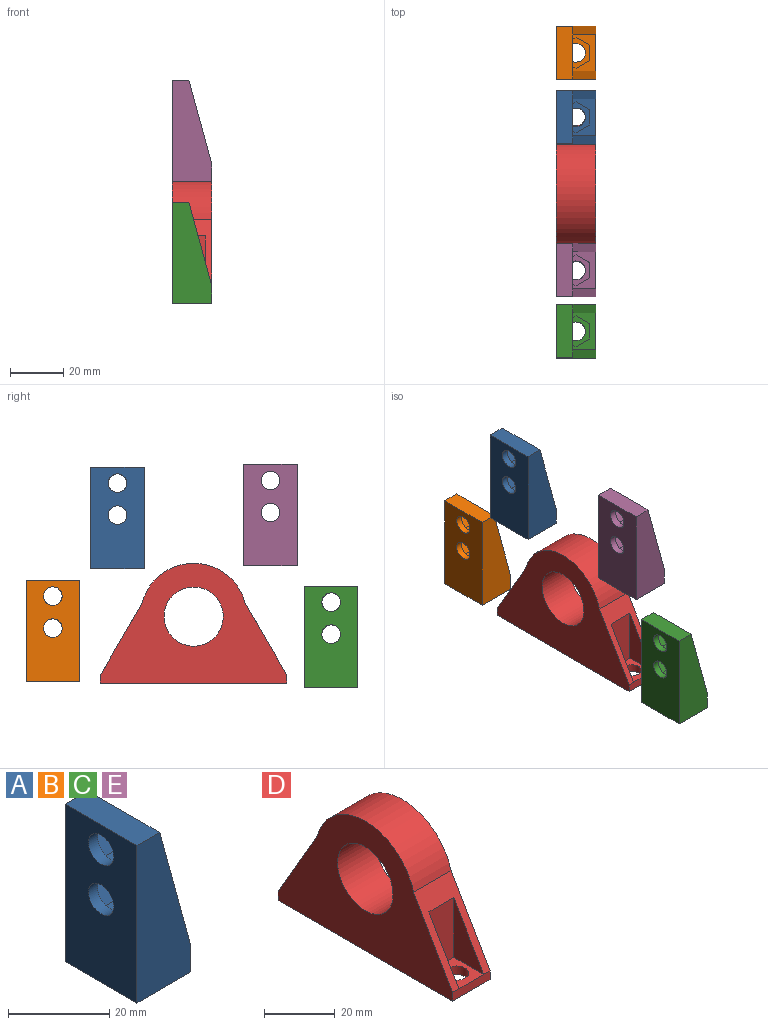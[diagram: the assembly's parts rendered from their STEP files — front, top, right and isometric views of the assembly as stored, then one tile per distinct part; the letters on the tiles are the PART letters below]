
ASSEMBLY  parts=5 mates=4
PART A: 39 faces, bbox 15x20x38 mm
  f0: plane 20x6.35mm, normal (1,0,0), area 127mm2, adj f1,f6,f33,f34,f37,f38
  f1: plane 14x12.46mm, normal (0,0,1), area 88.1mm2, adj f0,f2,f8,f9,f10,f11,f12,f35
  f2: plane 14x3.84mm, normal (1,0,0), area 53.8mm2, adj f1,f3,f7,f35,f36
  f3: plane 14x3.81mm, normal (0.71,0,-0.71), area 75.4mm2, adj f2,f4,f35,f36
  f4: plane 24x14mm, normal (1,0,0), area 162.8mm2, adj f3,f16,f17,f18,f19,f20,f21,f24
  f5: plane 38x20mm, normal (-1,0,0), area 683mm2, adj f6,f23,f31,f32,f34,f38
  f6: plane 20x15mm, normal (0,0,-1), area 261.5mm2, adj f0,f5,f15,f34,f38
  f7: plane 5.82x0.04mm, normal (0,0,-1), area 0.2mm2, adj f2,f8,f12,f13
  f8: plane 5x3.81mm, normal (0.5,0.87,0), area 22mm2, adj f1,f7,f9,f13,f14
  f9: plane 5x3.81mm, normal (-0.5,0.87,0), area 22mm2, adj f1,f8,f10,f14
  f10: plane 5.77x3.81mm, normal (-1,0,0), area 22mm2, adj f1,f9,f11,f14
  f11: plane 5x3.81mm, normal (-0.5,-0.87,0), area 22mm2, adj f1,f10,f12,f14
  f12: plane 5x3.81mm, normal (0.5,-0.87,0), area 22mm2, adj f1,f7,f11,f13,f14
  f13: plane 5.77x3.81mm, normal (1,0,0), area 22mm2, adj f7,f8,f12,f14
  f14: plane 11.55x10mm, normal (0,0,1), area 48.1mm2, adj f8,f9,f10,f11,f12,f13,f15
  f15: cylinder r=3.5mm len=7mm, axis (0,0,1), area 55.9mm2, adj f6,f14
  f16: plane 5x3.81mm, normal (0,-0.87,-0.5), area 22mm2, adj f4,f17,f21,f22
  f17: plane 5.77x3.81mm, normal (0,0,-1), area 22mm2, adj f4,f16,f18,f22
  f18: plane 5x3.81mm, normal (0,0.87,-0.5), area 22mm2, adj f4,f17,f19,f22
  f19: plane 5x3.81mm, normal (0,0.87,0.5), area 22mm2, adj f4,f18,f20,f22
  f20: plane 5.77x3.81mm, normal (0,0,1), area 22mm2, adj f4,f19,f21,f22
  f21: plane 5x3.81mm, normal (0,-0.87,0.5), area 22mm2, adj f4,f16,f20,f22
  f22: plane 11.55x10mm, normal (1,0,0), area 48.1mm2, adj f16,f17,f18,f19,f20,f21,f23
  f23: cylinder r=3.5mm len=7mm, axis (1,0,0), area 55.9mm2, adj f5,f22
  f24: plane 5x3.81mm, normal (0,-0.87,0.5), area 22mm2, adj f4,f25,f29,f30
  f25: plane 5.77x3.81mm, normal (0,0,1), area 22mm2, adj f4,f24,f26,f30
  f26: plane 5x3.81mm, normal (0,0.87,0.5), area 22mm2, adj f4,f25,f27,f30
  f27: plane 5x3.81mm, normal (0,0.87,-0.5), area 22mm2, adj f4,f26,f28,f30
  f28: plane 5.77x3.81mm, normal (0,0,-1), area 22mm2, adj f4,f27,f29,f30
  f29: plane 5x3.81mm, normal (0,-0.87,-0.5), area 22mm2, adj f4,f24,f28,f30
  f30: plane 11.55x10mm, normal (1,0,0), area 48.1mm2, adj f24,f25,f26,f27,f28,f29,f31
  f31: cylinder r=3.5mm len=7mm, axis (1,0,0), area 55.9mm2, adj f5,f30
  f32: plane 20x6.35mm, normal (0,0,1), area 127mm2, adj f4,f5,f33,f34,f37,f38
  f33: plane 31.65x8.65mm, normal (0.96,0,0.26), area 98.4mm2, adj f0,f32,f34,f35
  f34: plane 38x15mm, normal (0,-1,0), area 433.1mm2, adj f0,f5,f6,f32,f33
  f35: plane 31.65x12.46mm, normal (0,1,0), area 158.8mm2, adj f1,f2,f3,f4,f33
  f36: plane 31.65x12.46mm, normal (0,-1,0), area 158.8mm2, adj f1,f2,f3,f4,f37
  f37: plane 31.65x8.65mm, normal (0.96,0,0.26), area 98.4mm2, adj f0,f32,f36,f38
  f38: plane 38x15mm, normal (0,1,0), area 433.1mm2, adj f0,f5,f6,f32,f37
PART B: same geometry as A
PART C: same geometry as A
PART D: 19 faces, bbox 15x70x45 mm
  f0: cylinder r=20mm len=38.73mm, axis (-1,0,0), area 790.9mm2, adj f2,f3,f4,f8
  f1: cylinder r=11.11mm len=22.23mm, axis (-1,0,0), area 1047.3mm2, adj f2,f3
  f2: plane 70x45mm, normal (1,0,0), area 1720.3mm2, adj f0,f1,f4,f5,f6,f7,f8
  f3: plane 70x45mm, normal (-1,0,0), area 1720.3mm2, adj f0,f1,f4,f5,f6,f7,f8
  f4: plane 27x15.64mm, normal (0,-0.87,0.5), area 228.5mm2, adj f0,f2,f3,f5,f14,f15,f16
  f5: plane 15x3mm, normal (0,-1,0), area 45mm2, adj f2,f3,f4,f6,f13
  f6: plane 70x15mm, normal (0,0,-1), area 973mm2, adj f2,f3,f5,f7,f17,f18
  f7: plane 15x3mm, normal (0,1,0), area 45mm2, adj f2,f3,f6,f8,f9
  f8: plane 27x15.64mm, normal (0,0.87,0.5), area 228.5mm2, adj f0,f2,f3,f7,f10,f11,f12
  f9: plane 12x10mm, normal (0,0,1), area 81.5mm2, adj f7,f10,f11,f12,f18
  f10: plane 20.72x12mm, normal (1,0,0), area 124.3mm2, adj f8,f9,f11
  f11: plane 20.72x10mm, normal (0,1,0), area 207.2mm2, adj f8,f9,f10,f12
  f12: plane 20.72x12mm, normal (-1,0,0), area 124.3mm2, adj f8,f9,f11
  f13: plane 12x10mm, normal (0,0,1), area 81.5mm2, adj f5,f14,f15,f16,f17
  f14: plane 20.72x12mm, normal (-1,0,0), area 124.3mm2, adj f4,f13,f15
  f15: plane 20.72x10mm, normal (0,-1,0), area 207.2mm2, adj f4,f13,f14,f16
  f16: plane 20.72x12mm, normal (1,0,0), area 124.3mm2, adj f4,f13,f15
  f17: cylinder r=3.5mm len=7mm, axis (0,0,1), area 66mm2, adj f6,f13
  f18: cylinder r=3.5mm len=7mm, axis (0,0,1), area 66mm2, adj f6,f9
PART E: same geometry as A
PLACE A t=(0,28.57,18.01)mm
PLACE B t=(0,52.83,-24.36)mm
PLACE C t=(0,-51.61,-26.62)mm
PLACE D at identity fixed
PLACE E t=(0,-28.8,19.06)mm
MATE planar C.f5 <-> D.f3  axis (-1,0,0) through (0,-51.61,-8.41)mm
MATE planar D.f3 <-> B.f5  axis (-1,0,0) through (0,0,-8.41)mm
MATE planar E.f5 <-> D.f3  axis (-1,0,0) through (0,-28.8,37.27)mm
MATE planar B.f5 <-> D.f3  axis (-1,0,0) through (0,42.83,13.64)mm
